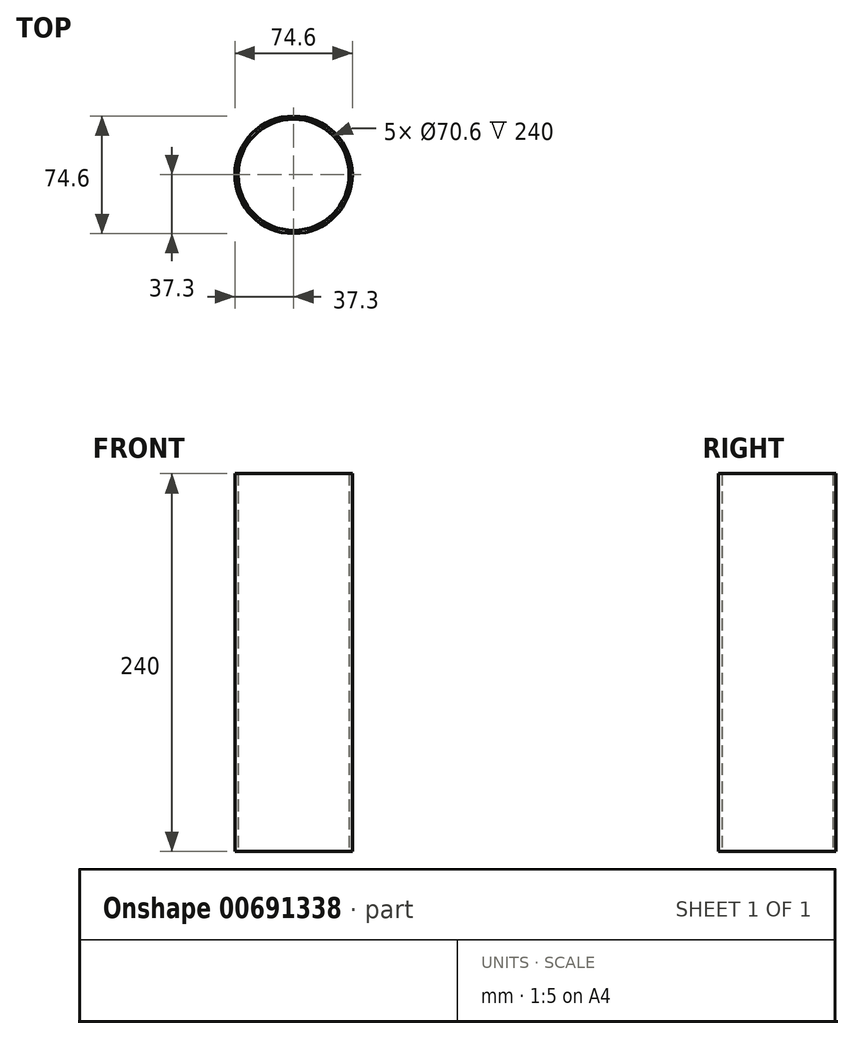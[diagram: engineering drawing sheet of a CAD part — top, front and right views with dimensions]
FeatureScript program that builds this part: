
annotation { "Feature Type Name" : "Feature", "Feature Type Description" : "" }
export const myFeature = defineFeature(function(context is Context, id is Id, definition is map)
    precondition{}
    {
        {
            var Q0;
            Q0=qCreatedBy(makeId("Top.planeOp"),FACE);
            var sketch = newSketch(context, id + "F0", { "sketchPlane" : qUnion([Q0])});
            skCircle(sketch, "E0", {"center": v(0, 0) * mm, "radius": 35.3 * mm});
            skCircle(sketch, "E1.0", {"center": v(0, 0) * mm, "radius": 37.3 * mm});
            skSolve(sketch);
        }
        {
            var Q0;
            Q0 = qSketchRegion(id + "F0", true);
            extrude(context, id + "F1", {"entities" : qUnion([Q0]), "depth" : 240 * mm, "offsetDistance" : 25 * mm});
        }
    });
